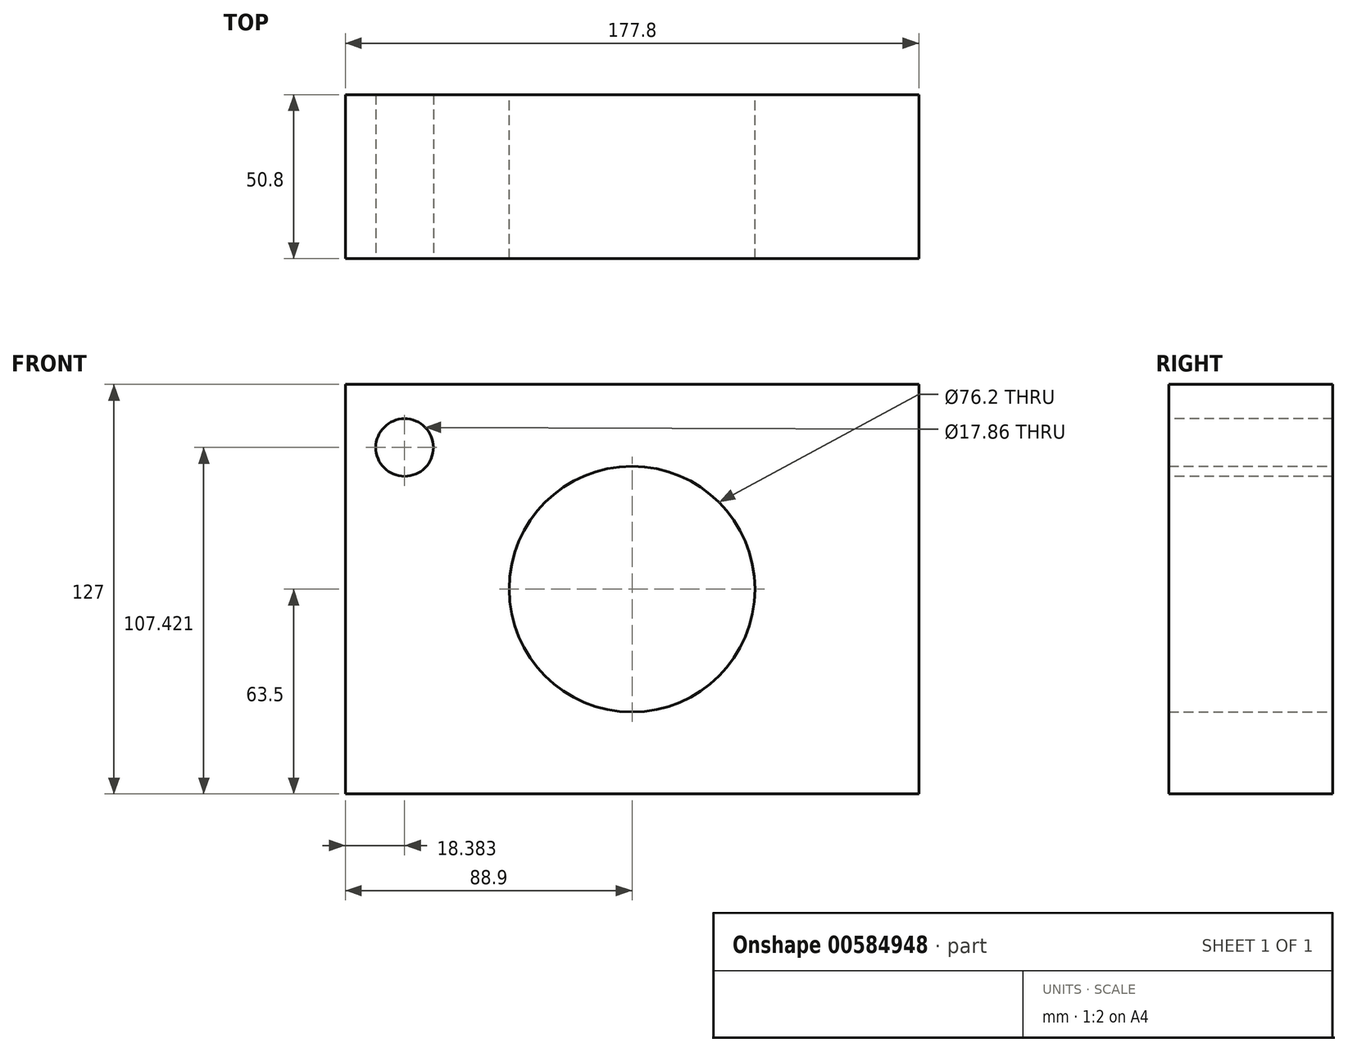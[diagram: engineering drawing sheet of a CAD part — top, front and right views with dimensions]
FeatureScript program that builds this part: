
annotation { "Feature Type Name" : "Feature", "Feature Type Description" : "" }
export const myFeature = defineFeature(function(context is Context, id is Id, definition is map)
    precondition{}
    {
        {
            var Q0;
            Q0=qCreatedBy(makeId("Front.planeOp"),FACE);
            var sketch = newSketch(context, id + "F0", { "sketchPlane" : qUnion([Q0])});
            skLineSegment(sketch, "E0.bottom", {"start": v(88.9, 63.5) * mm, "end": v(-88.9, 63.5) * mm});
            skLineSegment(sketch, "E0.top", {"start": v(88.9, -63.5) * mm, "end": v(-88.9, -63.5) * mm});
            skLineSegment(sketch, "E0.left", {"start": v(88.9, 63.5) * mm, "end": v(88.9, -63.5) * mm});
            skLineSegment(sketch, "E0.right", {"start": v(-88.9, 63.5) * mm, "end": v(-88.9, -63.5) * mm});
            skPoint(sketch, "E0.middle", {"position": v(0, 0) * mm});
            skSolve(sketch);
        }
        {
            var Q0;
            Q0=makeQuery(id+"F0.imprint","IMPRINT",FACE,{"disambiguationData":[TD([[makeQuery(id+"F0.imprint","IMPRINT",EDGE,{"derivedFrom":sQuery(id+"F0.wireOp",EDGE,"E0.bottom")}),1.0]])]});
            extrude(context, id + "F1", {"entities" : qUnion([Q0]), "endBound" : BoundingType.SYMMETRIC, "depth" : 50.8 * mm, "offsetDistance" : 25.4 * mm});
        }
        {
            var Q0;
            Q0=makeQuery(id+"F1.opExtrude","CAP_FACE",FACE,{"disambiguationData":[OSD([sQuery(id+"F0.wireOp",EDGE,"E0.bottom"),sQuery(id+"F0.wireOp",EDGE,"E0.top"),sQuery(id+"F0.wireOp",EDGE,"E0.left"),sQuery(id+"F0.wireOp",EDGE,"E0.right")])],"isStart":true});
            var sketch = newSketch(context, id + "F2", { "sketchPlane" : qUnion([Q0])});
            skCircle(sketch, "E1", {"center": v(0, 0) * mm, "radius": 38.1 * mm});
            skSolve(sketch);
        }
        {
            var Q0;
            Q0 = qSketchRegion(id + "F2", true);
            extrude(context, id + "F3", {"entities" : qUnion([Q0]), "operationType" : NewBodyOperationType.REMOVE, "endBound" : BoundingType.THROUGH_ALL, "oppositeDirection" : true, "depth" : 25.4 * mm, "offsetDistance" : 25.4 * mm});
        }
        {
            var Q0;
            Q0=makeQuery(id+"F1.opExtrude","CAP_FACE",FACE,{"disambiguationData":[OSD([sQuery(id+"F0.wireOp",EDGE,"E0.bottom"),sQuery(id+"F0.wireOp",EDGE,"E0.top"),sQuery(id+"F0.wireOp",EDGE,"E0.left"),sQuery(id+"F0.wireOp",EDGE,"E0.right")])],"isStart":false});
            var sketch = newSketch(context, id + "F4", { "sketchPlane" : qUnion([Q0])});
            skCircle(sketch, "E2", {"center": v(-70.52, 43.92) * mm, "radius": 8.93 * mm});
            skSolve(sketch);
        }
        {
            var Q0;
            Q0 = qSketchRegion(id + "F4", true);
            extrude(context, id + "F5", {"entities" : qUnion([Q0]), "operationType" : NewBodyOperationType.REMOVE, "endBound" : BoundingType.THROUGH_ALL, "oppositeDirection" : true, "depth" : 25.4 * mm, "offsetDistance" : 25.4 * mm});
        }
    });
